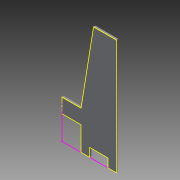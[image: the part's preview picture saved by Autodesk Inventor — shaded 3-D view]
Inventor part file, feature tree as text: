
AUTODESK INVENTOR PART (.ipt)
format: ipt  version: 2013 (Build 170138000, 138)  size: 108,544 bytes
history: native  units: mm
features: sketch x4, extrude x2
ambient origin geometry x8: Origin, YZ Plane, XZ Plane, XY Plane, X Axis, Y Axis, Z Axis, Center Point
bodies: Solid1 (feature_tree)
feature tree (6):
  extrude  "Extrusion1"  Depth=200.0mm
  sketch  "Sketch2"  dims[d6=20.0mm d7=0.0mm d8=370.0mm]
  sketch  "Sketch3"  dims[d9=150.0mm]
  extrude  "Extrusion3"  Depth=370.0mm
  sketch  "Sketch1"  dims[d2=1200.0mm d4=200.0mm]
  sketch  "Sketch5"  dims[d10=250.0mm d11=90.0mm d12=90.0mm d13=190.0mm d14=240.0mm d18=8.0mm d19=10.0mm d20=0.0mm d21=8.0mm d22=1190.0mm]
